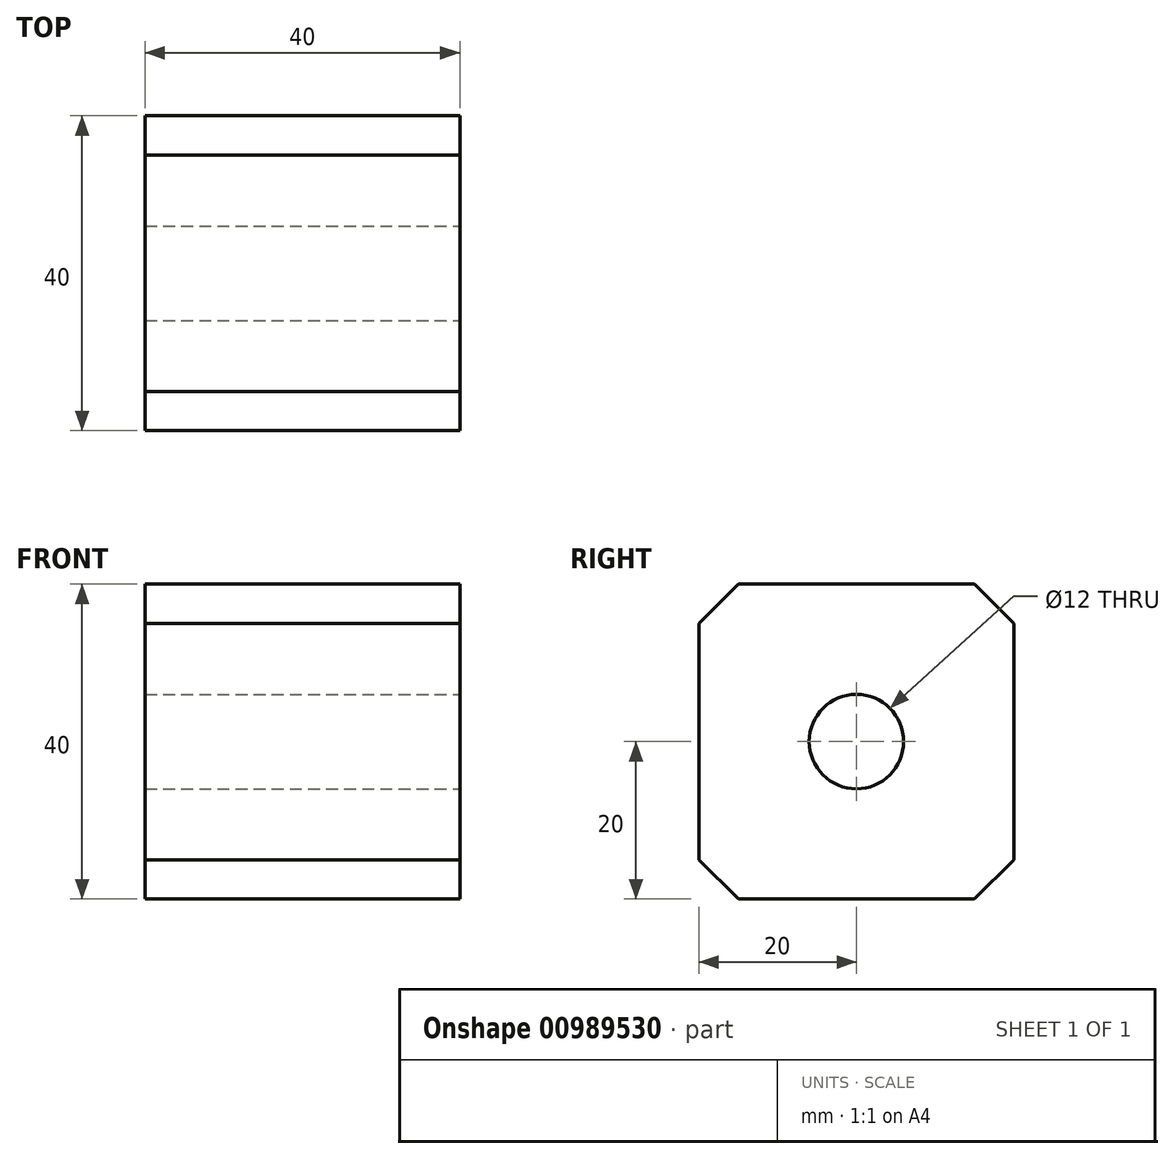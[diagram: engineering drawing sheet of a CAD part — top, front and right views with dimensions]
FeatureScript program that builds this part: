
annotation { "Feature Type Name" : "Feature", "Feature Type Description" : "" }
export const myFeature = defineFeature(function(context is Context, id is Id, definition is map)
    precondition{}
    {
        {
            var Q0;
            Q0=qCreatedBy(makeId("Right.planeOp"),FACE);
            var sketch = newSketch(context, id + "F0", { "sketchPlane" : qUnion([Q0])});
            skLineSegment(sketch, "E0.bottom", {"start": v(-20, 20) * mm, "end": v(20, 20) * mm});
            skLineSegment(sketch, "E0.top", {"start": v(-20, -20) * mm, "end": v(20, -20) * mm});
            skLineSegment(sketch, "E0.left", {"start": v(-20, 20) * mm, "end": v(-20, -20) * mm});
            skLineSegment(sketch, "E0.right", {"start": v(20, 20) * mm, "end": v(20, -20) * mm});
            skPoint(sketch, "E1", {"position": v(0, 0) * mm});
            skCircle(sketch, "E2", {"center": v(0, 0) * mm, "radius": 6 * mm});
            skSolve(sketch);
        }
        {
            var Q0;
            Q0=makeQuery(id+"F0.imprint","IMPRINT",FACE,{"disambiguationData":[TD([[makeQuery(id+"F0.imprint","IMPRINT",EDGE,{"derivedFrom":sQuery(id+"F0.wireOp",EDGE,"E0.bottom")}),-1.0]])]});
            extrude(context, id + "F1", {"entities" : qUnion([Q0]), "oppositeDirection" : true, "depth" : 40 * mm, "offsetDistance" : 25 * mm});
        }
        {
            var Q0;
            Q0=makeQuery(id+"F1.opExtrude","SWEPT_EDGE",EDGE,{"disambiguationData":[OSD([sQuery(id+"F0.wireOp",EDGE,"E0.bottom"),sQuery(id+"F0.wireOp",EDGE,"E0.left")])]});
            var Q1;
            Q1=makeQuery(id+"F1.opExtrude","SWEPT_EDGE",EDGE,{"disambiguationData":[OSD([sQuery(id+"F0.wireOp",EDGE,"E0.bottom"),sQuery(id+"F0.wireOp",EDGE,"E0.right")])]});
            var Q2;
            Q2=makeQuery(id+"F1.opExtrude","SWEPT_EDGE",EDGE,{"disambiguationData":[OSD([sQuery(id+"F0.wireOp",EDGE,"E0.top"),sQuery(id+"F0.wireOp",EDGE,"E0.left")])]});
            var Q3;
            Q3=makeQuery(id+"F1.opExtrude","SWEPT_EDGE",EDGE,{"disambiguationData":[OSD([sQuery(id+"F0.wireOp",EDGE,"E0.top"),sQuery(id+"F0.wireOp",EDGE,"E0.right")])]});
            chamfer(context, id + "F2", {"entities" : qUnion([Q0, Q1, Q2, Q3]), "width" : 5 * mm, "tangentPropagation" : true});
        }
    });
